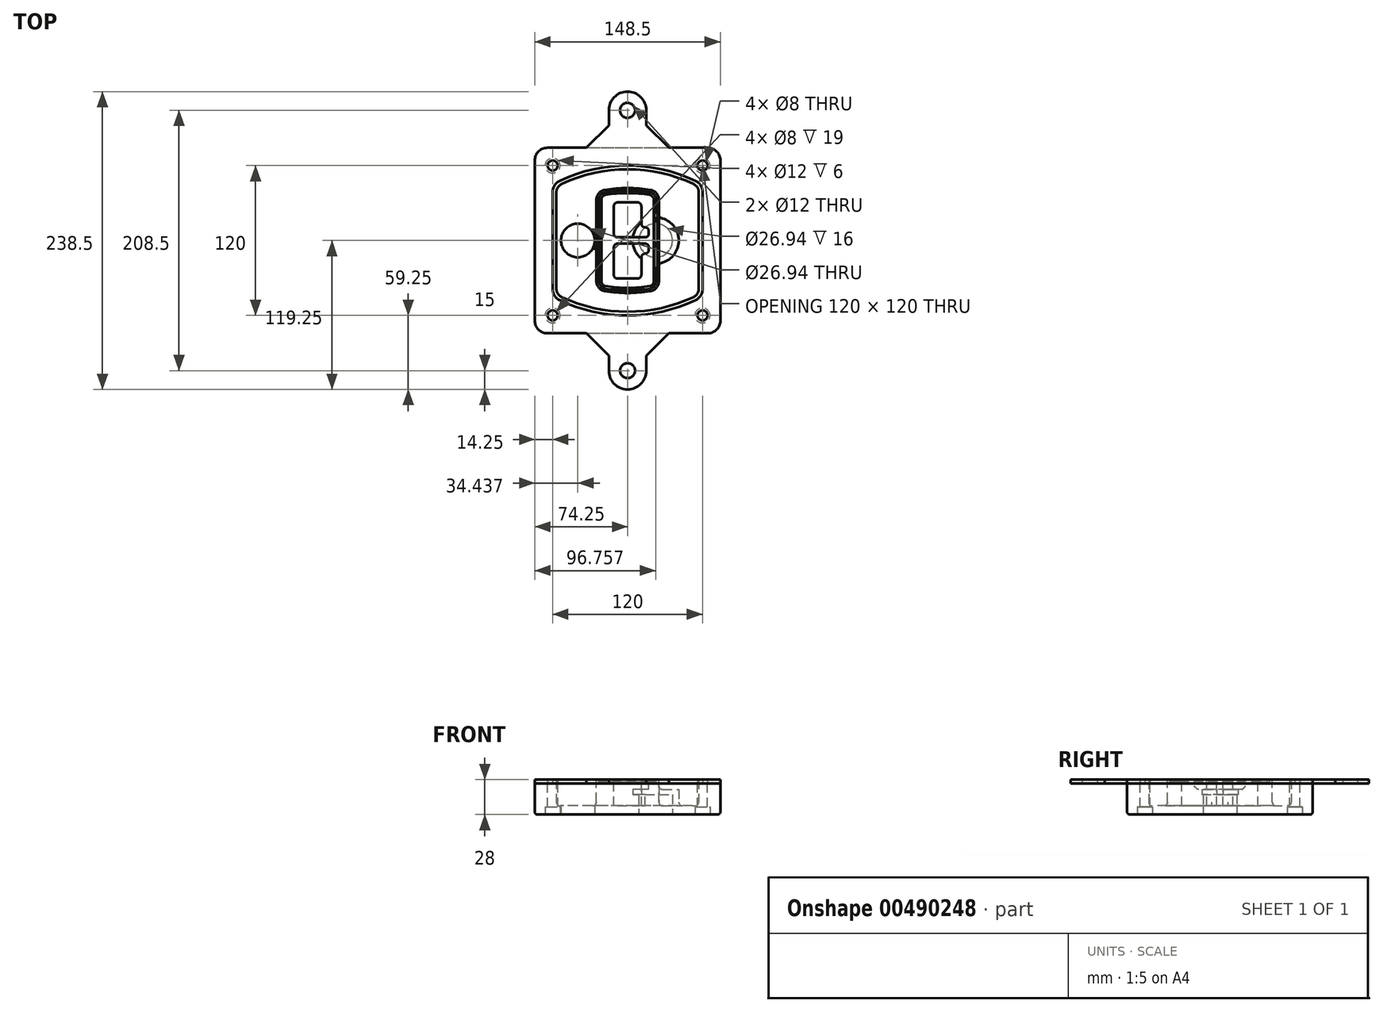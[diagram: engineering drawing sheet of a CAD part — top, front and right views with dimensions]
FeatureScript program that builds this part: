
annotation { "Feature Type Name" : "Feature", "Feature Type Description" : "" }
export const myFeature = defineFeature(function(context is Context, id is Id, definition is map)
    precondition{}
    {
        {
            var Q0;
            Q0=qCreatedBy(makeId("Top.planeOp"),FACE);
            var sketch = newSketch(context, id + "F0", { "sketchPlane" : qUnion([Q0])});
            skPoint(sketch, "E0.rect.middle", {"position": v(0, 0) * mm});
            skLineSegment(sketch, "E1.bottom", {"start": v(-64.25, -74.25) * mm, "end": v(64.25, -74.25) * mm});
            skLineSegment(sketch, "E1.top", {"start": v(-64.25, 74.25) * mm, "end": v(64.25, 74.25) * mm});
            skLineSegment(sketch, "E1.left", {"start": v(-74.25, -64.25) * mm, "end": v(-74.25, 64.25) * mm});
            skLineSegment(sketch, "E1.right", {"start": v(74.25, -64.25) * mm, "end": v(74.25, 64.25) * mm});
            skLineSegment(sketch, "E2", {"start": v(-74.25, 74.25) * mm, "end": v(74.25, -74.25) * mm, "construction": true});
            skLineSegment(sketch, "E3", {"start": v(74.25, 74.25) * mm, "end": v(-74.25, -74.25) * mm, "construction": true});
            skCircle(sketch, "E4", {"center": v(-60, 60) * mm, "radius": 4 * mm});
            skCircle(sketch, "E5", {"center": v(60, 60) * mm, "radius": 4 * mm});
            skCircle(sketch, "E6", {"center": v(60, -60) * mm, "radius": 4 * mm});
            skCircle(sketch, "E7", {"center": v(-60, -60) * mm, "radius": 4 * mm});
            skLineSegment(sketch, "E8", {"start": v(-60, 60) * mm, "end": v(60, 60) * mm, "construction": true});
            skLineSegment(sketch, "E9", {"start": v(60, 60) * mm, "end": v(60, -60) * mm, "construction": true});
            skLineSegment(sketch, "E10", {"start": v(60, -60) * mm, "end": v(-60, -60) * mm, "construction": true});
            skLineSegment(sketch, "E11", {"start": v(-60, -60) * mm, "end": v(-60, 60) * mm, "construction": true});
            skLineSegment(sketch, "E12", {"start": v(-60, 38.83) * mm, "end": v(-60, -38.83) * mm});
            skLineSegment(sketch, "E13", {"start": v(60, 38.83) * mm, "end": v(60, -38.83) * mm});
            skArc(sketch, "E14", {"start": v(54.26, 47.88) * mm, "mid": v(0, 60) * mm, "end": v(-54.26, 47.88) * mm});
            skArc(sketch, "E15", {"start": v(-54.26, -47.88) * mm, "mid": v(0, -60) * mm, "end": v(54.26, -47.88) * mm});
            skLineSegment(sketch, "E16", {"start": v(-60, 0) * mm, "end": v(60, 0) * mm, "construction": true});
            skPoint(sketch, "E17.visualSharp", {"position": v(-60, -45) * mm});
            skArc(sketch, "E17.filletArc", {"start": v(-60, -38.83) * mm, "mid": v(-58.44, -44.2) * mm, "end": v(-54.26, -47.88) * mm});
            skPoint(sketch, "E18.visualSharp", {"position": v(-60, 45) * mm});
            skArc(sketch, "E18.filletArc", {"start": v(-54.26, 47.88) * mm, "mid": v(-58.44, 44.2) * mm, "end": v(-60, 38.83) * mm});
            skPoint(sketch, "E19.visualSharp", {"position": v(60, 45) * mm});
            skArc(sketch, "E19.filletArc", {"start": v(60, 38.83) * mm, "mid": v(58.44, 44.2) * mm, "end": v(54.26, 47.88) * mm});
            skPoint(sketch, "E20.visualSharp", {"position": v(60, -45) * mm});
            skArc(sketch, "E20.filletArc", {"start": v(54.26, -47.88) * mm, "mid": v(58.44, -44.2) * mm, "end": v(60, -38.83) * mm});
            skPoint(sketch, "E21.visualSharp", {"position": v(-74.25, 74.25) * mm});
            skArc(sketch, "E21.filletArc", {"start": v(-64.25, 74.25) * mm, "mid": v(-71.32, 71.32) * mm, "end": v(-74.25, 64.25) * mm});
            skPoint(sketch, "E22.visualSharp", {"position": v(74.25, 74.25) * mm});
            skArc(sketch, "E22.filletArc", {"start": v(74.25, 64.25) * mm, "mid": v(71.32, 71.32) * mm, "end": v(64.25, 74.25) * mm});
            skPoint(sketch, "E23.visualSharp", {"position": v(74.25, -74.25) * mm});
            skArc(sketch, "E23.filletArc", {"start": v(64.25, -74.25) * mm, "mid": v(71.32, -71.32) * mm, "end": v(74.25, -64.25) * mm});
            skPoint(sketch, "E24.visualSharp", {"position": v(-74.25, -74.25) * mm});
            skArc(sketch, "E24.filletArc", {"start": v(-74.25, -64.25) * mm, "mid": v(-71.32, -71.32) * mm, "end": v(-64.25, -74.25) * mm});
            skArc(sketch, "E25.0", {"start": v(57, 38.83) * mm, "mid": v(55.9, 42.58) * mm, "end": v(52.98, 45.17) * mm});
            skLineSegment(sketch, "E25.1", {"start": v(57, 38.83) * mm, "end": v(57, -38.83) * mm});
            skArc(sketch, "E25.2", {"start": v(52.98, -45.17) * mm, "mid": v(55.9, -42.58) * mm, "end": v(57, -38.83) * mm});
            skArc(sketch, "E25.3", {"start": v(-52.98, -45.17) * mm, "mid": v(0, -57) * mm, "end": v(52.98, -45.17) * mm});
            skArc(sketch, "E25.4", {"start": v(-57, -38.83) * mm, "mid": v(-55.9, -42.58) * mm, "end": v(-52.98, -45.17) * mm});
            skArc(sketch, "E25.5", {"start": v(52.98, 45.17) * mm, "mid": v(0, 57) * mm, "end": v(-52.98, 45.17) * mm});
            skLineSegment(sketch, "E25.6", {"start": v(-57, 38.83) * mm, "end": v(-57, -38.83) * mm});
            skArc(sketch, "E25.7", {"start": v(-52.98, 45.17) * mm, "mid": v(-55.9, 42.58) * mm, "end": v(-57, 38.83) * mm});
            skArc(sketch, "E26.0", {"start": v(-55.96, 51.5) * mm, "mid": v(-61.82, 46.33) * mm, "end": v(-64, 38.83) * mm});
            skArc(sketch, "E26.1", {"start": v(55.96, 51.5) * mm, "mid": v(0, 64) * mm, "end": v(-55.96, 51.5) * mm});
            skArc(sketch, "E26.2", {"start": v(64, 38.83) * mm, "mid": v(61.82, 46.33) * mm, "end": v(55.96, 51.5) * mm});
            skLineSegment(sketch, "E26.3", {"start": v(64, 38.83) * mm, "end": v(64, -38.83) * mm});
            skArc(sketch, "E26.4", {"start": v(55.96, -51.5) * mm, "mid": v(61.82, -46.33) * mm, "end": v(64, -38.83) * mm});
            skLineSegment(sketch, "E26.5", {"start": v(-64, 38.83) * mm, "end": v(-64, -38.83) * mm});
            skArc(sketch, "E26.6", {"start": v(-55.96, -51.5) * mm, "mid": v(0, -64) * mm, "end": v(55.96, -51.5) * mm});
            skArc(sketch, "E26.7", {"start": v(-64, -38.83) * mm, "mid": v(-61.82, -46.33) * mm, "end": v(-55.96, -51.5) * mm});
            skSolve(sketch);
        }
        {
            var Q0;
            Q0=makeQuery(id+"F0.imprint","IMPRINT",FACE,{"disambiguationData":[TD([[makeQuery(id+"F0.imprint","IMPRINT",EDGE,{"derivedFrom":sQuery(id+"F0.wireOp",EDGE,"E1.bottom")}),1.0]])]});
            var Q1;
            Q1=makeQuery(id+"F0.imprint","IMPRINT",FACE,{"disambiguationData":[TD([[makeQuery(id+"F0.imprint","IMPRINT",EDGE,{"derivedFrom":sQuery(id+"F0.wireOp",EDGE,"E12")}),1.0]])]});
            var Q2;
            Q2=makeQuery(id+"F0.imprint","IMPRINT",FACE,{"disambiguationData":[TD([[makeQuery(id+"F0.imprint","IMPRINT",EDGE,{"derivedFrom":sQuery(id+"F0.wireOp",EDGE,"E25.0")}),1.0]])]});
            var Q3;
            Q3=makeQuery(id+"F0.imprint","IMPRINT",FACE,{"disambiguationData":[TD([[makeQuery(id+"F0.imprint","IMPRINT",EDGE,{"derivedFrom":sQuery(id+"F0.wireOp",EDGE,"E12")}),-1.0]])]});
            extrude(context, id + "F1", {"entities" : qUnion([Q0, Q1, Q2, Q3]), "oppositeDirection" : true, "depth" : 25 * mm});
        }
        {
            var Q0;
            Q0=makeQuery(id+"F0.imprint","IMPRINT",FACE,{"disambiguationData":[TD([[makeQuery(id+"F0.imprint","IMPRINT",EDGE,{"derivedFrom":sQuery(id+"F0.wireOp",EDGE,"E12")}),1.0]])]});
            extrude(context, id + "F2", {"entities" : qUnion([Q0]), "operationType" : NewBodyOperationType.ADD, "depth" : 3 * mm});
        }
        {
            var Q0;
            Q0=makeQuery(id+"F0.imprint","IMPRINT",FACE,{"disambiguationData":[TD([[makeQuery(id+"F0.imprint","IMPRINT",EDGE,{"derivedFrom":sQuery(id+"F0.wireOp",EDGE,"E25.0")}),1.0]])]});
            extrude(context, id + "F3", {"entities" : qUnion([Q0]), "operationType" : NewBodyOperationType.REMOVE, "oppositeDirection" : true, "depth" : 18 * mm});
        }
        {
            var Q0;
            Q0=makeQuery(id+"F2.opExtrude","CAP_FACE",FACE,{"disambiguationData":[OSD([sQuery(id+"F0.wireOp",EDGE,"E12"),sQuery(id+"F0.wireOp",EDGE,"E13"),sQuery(id+"F0.wireOp",EDGE,"E14"),sQuery(id+"F0.wireOp",EDGE,"E15"),sQuery(id+"F0.wireOp",EDGE,"E17.filletArc"),sQuery(id+"F0.wireOp",EDGE,"E18.filletArc"),sQuery(id+"F0.wireOp",EDGE,"E19.filletArc"),sQuery(id+"F0.wireOp",EDGE,"E20.filletArc"),sQuery(id+"F0.wireOp",EDGE,"E25.0"),sQuery(id+"F0.wireOp",EDGE,"E25.1"),sQuery(id+"F0.wireOp",EDGE,"E25.2"),sQuery(id+"F0.wireOp",EDGE,"E25.3"),sQuery(id+"F0.wireOp",EDGE,"E25.4"),sQuery(id+"F0.wireOp",EDGE,"E25.5"),sQuery(id+"F0.wireOp",EDGE,"E25.6"),sQuery(id+"F0.wireOp",EDGE,"E25.7")])],"isStart":false});
            var sketch = newSketch(context, id + "F4", { "sketchPlane" : qUnion([Q0])});
            skArc(sketch, "E27.0", {"start": v(-18.34, -40.45) * mm, "mid": v(0, -42) * mm, "end": v(18.34, -40.45) * mm});
            skArc(sketch, "E28.0", {"start": v(18.34, 40.45) * mm, "mid": v(0, 42) * mm, "end": v(-18.34, 40.45) * mm});
            skLineSegment(sketch, "E29", {"start": v(-25, 32.57) * mm, "end": v(-25, -32.57) * mm});
            skLineSegment(sketch, "E30", {"start": v(25, 32.57) * mm, "end": v(25, -32.57) * mm});
            skLineSegment(sketch, "E31", {"start": v(-25, 39.1) * mm, "end": v(25, 39.1) * mm, "construction": true});
            skLineSegment(sketch, "E32", {"start": v(-25, -39.1) * mm, "end": v(25, -39.1) * mm, "construction": true});
            skPoint(sketch, "E33.visualSharp", {"position": v(-25, 39.1) * mm});
            skArc(sketch, "E33.filletArc", {"start": v(-18.34, 40.45) * mm, "mid": v(-23.11, 37.73) * mm, "end": v(-25, 32.57) * mm});
            skPoint(sketch, "E34.visualSharp", {"position": v(25, 39.1) * mm});
            skArc(sketch, "E34.filletArc", {"start": v(25, 32.57) * mm, "mid": v(23.11, 37.73) * mm, "end": v(18.34, 40.45) * mm});
            skPoint(sketch, "E35.visualSharp", {"position": v(25, -39.1) * mm});
            skArc(sketch, "E35.filletArc", {"start": v(18.34, -40.45) * mm, "mid": v(23.11, -37.73) * mm, "end": v(25, -32.57) * mm});
            skPoint(sketch, "E36.visualSharp", {"position": v(-25, -39.1) * mm});
            skArc(sketch, "E36.filletArc", {"start": v(-25, -32.57) * mm, "mid": v(-23.11, -37.73) * mm, "end": v(-18.34, -40.45) * mm});
            skArc(sketch, "E37.0", {"start": v(52.98, 45.17) * mm, "mid": v(0, 57) * mm, "end": v(-52.98, 45.17) * mm});
            skArc(sketch, "E37.1", {"start": v(-52.98, 45.17) * mm, "mid": v(-55.9, 42.58) * mm, "end": v(-57, 38.83) * mm});
            skLineSegment(sketch, "E37.2", {"start": v(-57, 38.83) * mm, "end": v(-57, -38.83) * mm});
            skArc(sketch, "E37.3", {"start": v(-57, -38.83) * mm, "mid": v(-55.9, -42.58) * mm, "end": v(-52.98, -45.17) * mm});
            skArc(sketch, "E37.4", {"start": v(-52.98, -45.17) * mm, "mid": v(0, -57) * mm, "end": v(52.98, -45.17) * mm});
            skArc(sketch, "E37.5", {"start": v(52.98, -45.17) * mm, "mid": v(55.9, -42.58) * mm, "end": v(57, -38.83) * mm});
            skLineSegment(sketch, "E37.6", {"start": v(57, 38.83) * mm, "end": v(57, -38.83) * mm});
            skArc(sketch, "E37.7", {"start": v(57, 38.83) * mm, "mid": v(55.9, 42.58) * mm, "end": v(52.98, 45.17) * mm});
            skLineSegment(sketch, "E38.0", {"start": v(23, 32.57) * mm, "end": v(23, -32.57) * mm});
            skArc(sketch, "E38.1", {"start": v(18, -38.48) * mm, "mid": v(21.58, -36.44) * mm, "end": v(23, -32.57) * mm});
            skArc(sketch, "E38.2", {"start": v(-18, -38.48) * mm, "mid": v(0, -40) * mm, "end": v(18, -38.48) * mm});
            skArc(sketch, "E38.3", {"start": v(-23, -32.57) * mm, "mid": v(-21.58, -36.44) * mm, "end": v(-18, -38.48) * mm});
            skLineSegment(sketch, "E38.4", {"start": v(-23, 32.57) * mm, "end": v(-23, -32.57) * mm});
            skArc(sketch, "E38.5", {"start": v(23, 32.57) * mm, "mid": v(21.58, 36.44) * mm, "end": v(18, 38.48) * mm});
            skArc(sketch, "E38.6", {"start": v(-18, 38.48) * mm, "mid": v(-21.58, 36.44) * mm, "end": v(-23, 32.57) * mm});
            skArc(sketch, "E38.7", {"start": v(18, 38.48) * mm, "mid": v(0, 40) * mm, "end": v(-18, 38.48) * mm});
            skArc(sketch, "E39.0", {"start": v(21, 32.57) * mm, "mid": v(20.06, 35.15) * mm, "end": v(17.67, 36.5) * mm});
            skLineSegment(sketch, "E39.1", {"start": v(21, 32.57) * mm, "end": v(21, -32.57) * mm});
            skArc(sketch, "E39.2", {"start": v(17.67, -36.5) * mm, "mid": v(20.06, -35.15) * mm, "end": v(21, -32.57) * mm});
            skArc(sketch, "E39.3", {"start": v(-17.67, -36.5) * mm, "mid": v(0, -38) * mm, "end": v(17.67, -36.5) * mm});
            skArc(sketch, "E39.4", {"start": v(-21, -32.57) * mm, "mid": v(-20.06, -35.15) * mm, "end": v(-17.67, -36.5) * mm});
            skArc(sketch, "E39.5", {"start": v(17.67, 36.5) * mm, "mid": v(0, 38) * mm, "end": v(-17.67, 36.5) * mm});
            skLineSegment(sketch, "E39.6", {"start": v(-21, 32.57) * mm, "end": v(-21, -32.57) * mm});
            skArc(sketch, "E39.7", {"start": v(-17.67, 36.5) * mm, "mid": v(-20.06, 35.15) * mm, "end": v(-21, 32.57) * mm});
            skLineSegment(sketch, "E40", {"start": v(-25, 0) * mm, "end": v(25, 0) * mm, "construction": true});
            skLineSegment(sketch, "E41", {"start": v(-11, 5.5) * mm, "end": v(-11, 27.5) * mm});
            skLineSegment(sketch, "E42", {"start": v(-8, 30.5) * mm, "end": v(8, 30.5) * mm});
            skLineSegment(sketch, "E43", {"start": v(11, 27.5) * mm, "end": v(11, 13.5) * mm});
            skLineSegment(sketch, "E44", {"start": v(14, 10.5) * mm, "end": v(14, 10.5) * mm});
            skLineSegment(sketch, "E45", {"start": v(17, 7.5) * mm, "end": v(17, 5.5) * mm});
            skLineSegment(sketch, "E46", {"start": v(14, 2.5) * mm, "end": v(-8, 2.5) * mm});
            skPoint(sketch, "E47.visualSharp", {"position": v(-11, 30.5) * mm});
            skArc(sketch, "E47.filletArc", {"start": v(-8, 30.5) * mm, "mid": v(-10.12, 29.62) * mm, "end": v(-11, 27.5) * mm});
            skPoint(sketch, "E48.visualSharp", {"position": v(11, 30.5) * mm});
            skArc(sketch, "E48.filletArc", {"start": v(11, 27.5) * mm, "mid": v(10.12, 29.62) * mm, "end": v(8, 30.5) * mm});
            skPoint(sketch, "E49.visualSharp", {"position": v(11, 10.5) * mm});
            skArc(sketch, "E49.filletArc", {"start": v(11, 13.5) * mm, "mid": v(11.88, 11.38) * mm, "end": v(14, 10.5) * mm});
            skPoint(sketch, "E50.visualSharp", {"position": v(17, 10.5) * mm});
            skArc(sketch, "E50.filletArc", {"start": v(17, 7.5) * mm, "mid": v(16.12, 9.62) * mm, "end": v(14, 10.5) * mm});
            skPoint(sketch, "E51.visualSharp", {"position": v(17, 2.5) * mm});
            skArc(sketch, "E51.filletArc", {"start": v(14, 2.5) * mm, "mid": v(16.12, 3.38) * mm, "end": v(17, 5.5) * mm});
            skPoint(sketch, "E52.visualSharp", {"position": v(-11, 2.5) * mm});
            skArc(sketch, "E52.filletArc", {"start": v(-11, 5.5) * mm, "mid": v(-10.12, 3.38) * mm, "end": v(-8, 2.5) * mm});
            skLineSegment(sketch, "E53.0.MirrorCS", {"start": v(14, -2.5) * mm, "end": v(-8, -2.5) * mm});
            skArc(sketch, "E54.0.MirrorCS", {"start": v(-11, -5.5) * mm, "mid": v(-10.12, -3.38) * mm, "end": v(-8, -2.5) * mm});
            skLineSegment(sketch, "E55.0.MirrorCS", {"start": v(-11, -5.5) * mm, "end": v(-11, -27.5) * mm});
            skArc(sketch, "E56.0.MirrorCS", {"start": v(-8, -30.5) * mm, "mid": v(-10.12, -29.62) * mm, "end": v(-11, -27.5) * mm});
            skLineSegment(sketch, "E57.0.MirrorCS", {"start": v(-8, -30.5) * mm, "end": v(8, -30.5) * mm});
            skArc(sketch, "E58.0.MirrorCS", {"start": v(11, -27.5) * mm, "mid": v(10.12, -29.62) * mm, "end": v(8, -30.5) * mm});
            skLineSegment(sketch, "E59.0.MirrorCS", {"start": v(11, -27.5) * mm, "end": v(11, -13.5) * mm});
            skArc(sketch, "E60.0.MirrorCS", {"start": v(11, -13.5) * mm, "mid": v(11.88, -11.38) * mm, "end": v(14, -10.5) * mm});
            skArc(sketch, "E61.0.MirrorCS", {"start": v(17, -7.5) * mm, "mid": v(16.12, -9.62) * mm, "end": v(14, -10.5) * mm});
            skLineSegment(sketch, "E62.0.MirrorCS", {"start": v(17, -7.5) * mm, "end": v(17, -5.5) * mm});
            skArc(sketch, "E63.0.MirrorCS", {"start": v(14, -2.5) * mm, "mid": v(16.12, -3.38) * mm, "end": v(17, -5.5) * mm});
            skSolve(sketch);
        }
        {
            var Q0;
            Q0=makeQuery(id+"F4.imprint","IMPRINT",FACE,{"disambiguationData":[TD([[makeQuery(id+"F4.imprint","IMPRINT",EDGE,{"derivedFrom":sQuery(id+"F4.wireOp",EDGE,"E27.0")}),1.0]])]});
            var Q1;
            Q1=makeQuery(id+"F4.imprint","IMPRINT",FACE,{"disambiguationData":[TD([[makeQuery(id+"F4.imprint","IMPRINT",EDGE,{"derivedFrom":sQuery(id+"F4.wireOp",EDGE,"E38.0")}),-1.0]])]});
            var Q2;
            Q2=makeQuery(id+"F4.imprint","IMPRINT",FACE,{"disambiguationData":[TD([[makeQuery(id+"F4.imprint","IMPRINT",EDGE,{"derivedFrom":sQuery(id+"F4.wireOp",EDGE,"E39.0")}),1.0]])]});
            extrude(context, id + "F5", {"entities" : qUnion([Q0, Q1, Q2]), "operationType" : NewBodyOperationType.ADD, "endBound" : BoundingType.UP_TO_NEXT, "oppositeDirection" : true, "depth" : 25 * mm});
        }
        {
            var Q0;
            Q0=makeQuery(id+"F4.imprint","IMPRINT",FACE,{"disambiguationData":[TD([[makeQuery(id+"F4.imprint","IMPRINT",EDGE,{"derivedFrom":sQuery(id+"F4.wireOp",EDGE,"E38.0")}),-1.0]])]});
            extrude(context, id + "F6", {"entities" : qUnion([Q0]), "operationType" : NewBodyOperationType.REMOVE, "oppositeDirection" : true, "depth" : 2 * mm});
        }
        {
            var Q0;
            Q0=makeQuery(id+"F1.opExtrude","CAP_FACE",FACE,{"disambiguationData":[OSD([sQuery(id+"F0.wireOp",EDGE,"E1.bottom"),sQuery(id+"F0.wireOp",EDGE,"E1.top"),sQuery(id+"F0.wireOp",EDGE,"E1.left"),sQuery(id+"F0.wireOp",EDGE,"E1.right"),sQuery(id+"F0.wireOp",EDGE,"E4"),sQuery(id+"F0.wireOp",EDGE,"E5"),sQuery(id+"F0.wireOp",EDGE,"E6"),sQuery(id+"F0.wireOp",EDGE,"E7"),sQuery(id+"F0.wireOp",EDGE,"E21.filletArc"),sQuery(id+"F0.wireOp",EDGE,"E22.filletArc"),sQuery(id+"F0.wireOp",EDGE,"E23.filletArc"),sQuery(id+"F0.wireOp",EDGE,"E24.filletArc")])],"isStart":false});
            var sketch = newSketch(context, id + "F7", { "sketchPlane" : qUnion([Q0])});
            skCircle(sketch, "E64", {"center": v(22.5, 0) * mm, "radius": 13.47 * mm});
            skCircle(sketch, "E65", {"center": v(-39.81, 0) * mm, "radius": 13.47 * mm});
            skLineSegment(sketch, "E66", {"start": v(74.25, 0) * mm, "end": v(-74.25, 0) * mm});
            skCircle(sketch, "E67", {"center": v(22.5, 0) * mm, "radius": 18.47 * mm});
            skCircle(sketch, "E68", {"center": v(60, -60) * mm, "radius": 6 * mm});
            skCircle(sketch, "E69", {"center": v(-60, -60) * mm, "radius": 6 * mm});
            skCircle(sketch, "E70", {"center": v(-60, 60) * mm, "radius": 6 * mm});
            skCircle(sketch, "E71", {"center": v(60, 60) * mm, "radius": 6 * mm});
            skSolve(sketch);
        }
        {
            var Q0;
            {var subQ1=sQuery(id+"F7.wireOp",EDGE,"E66");var subQ4=sQuery(id+"F7.wireOp",EDGE,"E64");var subQ6=makeQuery(id+"F7.imprint","INTERSECT",VERTEX,{"disambiguationData":[OD(0.0)],"derivedFrom":[subQ4,subQ1]});Q0=makeQuery(id+"F7.imprint","IMPRINT",FACE,{"disambiguationData":[TD([[makeQuery(id+"F7.imprint","IMPRINT",EDGE,{"disambiguationData":[TD([[subQ6,-1.0]])],"derivedFrom":subQ4}),-1.0]])]});}
            var Q1;
            {var subQ0=sQuery(id+"F7.wireOp",EDGE,"E66");var subQ1=sQuery(id+"F7.wireOp",EDGE,"E64");var subQ3=makeQuery(id+"F7.imprint","INTERSECT",VERTEX,{"disambiguationData":[OD(0.0)],"derivedFrom":[subQ1,subQ0]});Q1=makeQuery(id+"F7.imprint","IMPRINT",FACE,{"disambiguationData":[TD([[makeQuery(id+"F7.imprint","IMPRINT",EDGE,{"disambiguationData":[TD([[subQ3,-1.0]])],"derivedFrom":subQ1}),1.0]])]});}
            var Q2;
            {var subQ0=sQuery(id+"F7.wireOp",EDGE,"E66");var subQ1=sQuery(id+"F7.wireOp",EDGE,"E64");var subQ3=makeQuery(id+"F7.imprint","INTERSECT",VERTEX,{"disambiguationData":[OD(0.0)],"derivedFrom":[subQ1,subQ0]});Q2=makeQuery(id+"F7.imprint","IMPRINT",FACE,{"disambiguationData":[TD([[makeQuery(id+"F7.imprint","IMPRINT",EDGE,{"disambiguationData":[TD([[subQ3,1.0]])],"derivedFrom":subQ1}),1.0]])]});}
            var Q3;
            {var subQ1=sQuery(id+"F7.wireOp",EDGE,"E66");var subQ4=sQuery(id+"F7.wireOp",EDGE,"E64");var subQ6=makeQuery(id+"F7.imprint","INTERSECT",VERTEX,{"disambiguationData":[OD(0.0)],"derivedFrom":[subQ4,subQ1]});Q3=makeQuery(id+"F7.imprint","IMPRINT",FACE,{"disambiguationData":[TD([[makeQuery(id+"F7.imprint","IMPRINT",EDGE,{"disambiguationData":[TD([[subQ6,1.0]])],"derivedFrom":subQ4}),-1.0]])]});}
            extrude(context, id + "F8", {"entities" : qUnion([Q0, Q1, Q2, Q3]), "operationType" : NewBodyOperationType.ADD, "oppositeDirection" : true, "depth" : 20 * mm});
        }
        {
            var Q0;
            {var subQ0=sQuery(id+"F7.wireOp",EDGE,"E66");var subQ1=sQuery(id+"F7.wireOp",EDGE,"E64");var subQ3=makeQuery(id+"F7.imprint","INTERSECT",VERTEX,{"disambiguationData":[OD(0.0)],"derivedFrom":[subQ1,subQ0]});Q0=makeQuery(id+"F7.imprint","IMPRINT",FACE,{"disambiguationData":[TD([[makeQuery(id+"F7.imprint","IMPRINT",EDGE,{"disambiguationData":[TD([[subQ3,-1.0]])],"derivedFrom":subQ1}),1.0]])]});}
            var Q1;
            {var subQ0=sQuery(id+"F7.wireOp",EDGE,"E66");var subQ1=sQuery(id+"F7.wireOp",EDGE,"E64");var subQ3=makeQuery(id+"F7.imprint","INTERSECT",VERTEX,{"disambiguationData":[OD(0.0)],"derivedFrom":[subQ1,subQ0]});Q1=makeQuery(id+"F7.imprint","IMPRINT",FACE,{"disambiguationData":[TD([[makeQuery(id+"F7.imprint","IMPRINT",EDGE,{"disambiguationData":[TD([[subQ3,1.0]])],"derivedFrom":subQ1}),1.0]])]});}
            extrude(context, id + "F9", {"entities" : qUnion([Q0, Q1]), "operationType" : NewBodyOperationType.REMOVE, "oppositeDirection" : true, "depth" : 16 * mm});
        }
        {
            var Q0;
            {var subQ0=sQuery(id+"F7.wireOp",EDGE,"E66");var subQ1=sQuery(id+"F7.wireOp",EDGE,"E65");var subQ3=makeQuery(id+"F7.imprint","INTERSECT",VERTEX,{"disambiguationData":[OD(0.0)],"derivedFrom":[subQ1,subQ0]});Q0=makeQuery(id+"F7.imprint","IMPRINT",FACE,{"disambiguationData":[TD([[makeQuery(id+"F7.imprint","IMPRINT",EDGE,{"disambiguationData":[TD([[subQ3,-1.0]])],"derivedFrom":subQ1}),1.0]])]});}
            var Q1;
            {var subQ0=sQuery(id+"F7.wireOp",EDGE,"E66");var subQ1=sQuery(id+"F7.wireOp",EDGE,"E65");var subQ3=makeQuery(id+"F7.imprint","INTERSECT",VERTEX,{"disambiguationData":[OD(0.0)],"derivedFrom":[subQ1,subQ0]});Q1=makeQuery(id+"F7.imprint","IMPRINT",FACE,{"disambiguationData":[TD([[makeQuery(id+"F7.imprint","IMPRINT",EDGE,{"disambiguationData":[TD([[subQ3,1.0]])],"derivedFrom":subQ1}),1.0]])]});}
            extrude(context, id + "F10", {"entities" : qUnion([Q0, Q1]), "operationType" : NewBodyOperationType.REMOVE, "oppositeDirection" : true, "depth" : 25 * mm});
        }
        {
            var Q0;
            Q0=makeQuery(id+"F7.imprint","IMPRINT",FACE,{"disambiguationData":[TD([[makeQuery(id+"F7.imprint","IMPRINT",EDGE,{"derivedFrom":sQuery(id+"F7.wireOp",EDGE,"E68")}),1.0]])]});
            var Q1;
            Q1=makeQuery(id+"F7.imprint","IMPRINT",FACE,{"disambiguationData":[TD([[makeQuery(id+"F7.imprint","IMPRINT",EDGE,{"derivedFrom":makeQuery(id+"F1.opExtrude","CAP_EDGE",EDGE,{"disambiguationData":[OSD([sQuery(id+"F0.wireOp",EDGE,"E5")])],"isStart":false})}),-1.0]])]});
            var Q2;
            Q2=makeQuery(id+"F7.imprint","IMPRINT",FACE,{"disambiguationData":[TD([[makeQuery(id+"F7.imprint","IMPRINT",EDGE,{"derivedFrom":sQuery(id+"F7.wireOp",EDGE,"E69")}),1.0]])]});
            var Q3;
            Q3=makeQuery(id+"F7.imprint","IMPRINT",FACE,{"disambiguationData":[TD([[makeQuery(id+"F7.imprint","IMPRINT",EDGE,{"derivedFrom":makeQuery(id+"F1.opExtrude","CAP_EDGE",EDGE,{"disambiguationData":[OSD([sQuery(id+"F0.wireOp",EDGE,"E4")])],"isStart":false})}),-1.0]])]});
            var Q4;
            Q4=makeQuery(id+"F7.imprint","IMPRINT",FACE,{"disambiguationData":[TD([[makeQuery(id+"F7.imprint","IMPRINT",EDGE,{"derivedFrom":sQuery(id+"F7.wireOp",EDGE,"E70")}),1.0]])]});
            var Q5;
            Q5=makeQuery(id+"F7.imprint","IMPRINT",FACE,{"disambiguationData":[TD([[makeQuery(id+"F7.imprint","IMPRINT",EDGE,{"derivedFrom":makeQuery(id+"F1.opExtrude","CAP_EDGE",EDGE,{"disambiguationData":[OSD([sQuery(id+"F0.wireOp",EDGE,"E7")])],"isStart":false})}),-1.0]])]});
            var Q6;
            Q6=makeQuery(id+"F7.imprint","IMPRINT",FACE,{"disambiguationData":[TD([[makeQuery(id+"F7.imprint","IMPRINT",EDGE,{"derivedFrom":sQuery(id+"F7.wireOp",EDGE,"E71")}),1.0]])]});
            var Q7;
            Q7=makeQuery(id+"F7.imprint","IMPRINT",FACE,{"disambiguationData":[TD([[makeQuery(id+"F7.imprint","IMPRINT",EDGE,{"derivedFrom":makeQuery(id+"F1.opExtrude","CAP_EDGE",EDGE,{"disambiguationData":[OSD([sQuery(id+"F0.wireOp",EDGE,"E6")])],"isStart":false})}),-1.0]])]});
            extrude(context, id + "F11", {"entities" : qUnion([Q0, Q1, Q2, Q3, Q4, Q5, Q6, Q7]), "operationType" : NewBodyOperationType.REMOVE, "oppositeDirection" : true, "depth" : 6 * mm});
        }
        {
            var Q0;
            Q0=makeQuery(id+"F9.boolean.opBoolean","COPY",FACE,{"derivedFrom":makeQuery(id+"F9.opExtrude","CAP_FACE",FACE,{"disambiguationData":[OSD([sQuery(id+"F7.wireOp",EDGE,"E64")])],"isStart":false})});
            var sketch = newSketch(context, id + "F12", { "sketchPlane" : qUnion([Q0])});
            skArc(sketch, "E72.0", {"start": v(11, 14.45) * mm, "mid": v(6.45, 9.13) * mm, "end": v(4.2, 2.5) * mm});
            skArc(sketch, "E72.1", {"start": v(4.2, -2.5) * mm, "mid": v(6.45, -9.13) * mm, "end": v(11, -14.45) * mm});
            skLineSegment(sketch, "E73", {"start": v(4.2, -2.5) * mm, "end": v(14, -2.5) * mm});
            skLineSegment(sketch, "E74.0", {"start": v(14, 2.5) * mm, "end": v(4.2, 2.5) * mm});
            skArc(sketch, "E74.1", {"start": v(14, 2.5) * mm, "mid": v(16.12, 3.38) * mm, "end": v(17, 5.5) * mm});
            skLineSegment(sketch, "E74.2", {"start": v(17, 7.5) * mm, "end": v(17, 5.5) * mm});
            skArc(sketch, "E74.3", {"start": v(17, 7.5) * mm, "mid": v(16.12, 9.62) * mm, "end": v(14, 10.5) * mm});
            skArc(sketch, "E74.4", {"start": v(11, 13.5) * mm, "mid": v(11.88, 11.38) * mm, "end": v(14, 10.5) * mm});
            skLineSegment(sketch, "E74.5", {"start": v(11, 14.45) * mm, "end": v(11, 13.5) * mm});
            skLineSegment(sketch, "E74.7", {"start": v(14, -2.5) * mm, "end": v(4.2, -2.5) * mm});
            skArc(sketch, "E74.8", {"start": v(14, -2.5) * mm, "mid": v(16.12, -3.38) * mm, "end": v(17, -5.5) * mm});
            skLineSegment(sketch, "E74.9", {"start": v(17, -7.5) * mm, "end": v(17, -5.5) * mm});
            skArc(sketch, "E74.10", {"start": v(17, -7.5) * mm, "mid": v(16.12, -9.62) * mm, "end": v(14, -10.5) * mm});
            skArc(sketch, "E74.11", {"start": v(11, -13.5) * mm, "mid": v(11.88, -11.38) * mm, "end": v(14, -10.5) * mm});
            skLineSegment(sketch, "E74.12", {"start": v(11, -14.45) * mm, "end": v(11, -13.5) * mm});
            skPoint(sketch, "E75.orphan", {"position": v(11, -27.5) * mm});
            skPoint(sketch, "E76.orphan", {"position": v(-8, -2.5) * mm});
            skPoint(sketch, "E77.orphan", {"position": v(-8, 2.5) * mm});
            skPoint(sketch, "E78.orphan", {"position": v(11, 27.5) * mm});
            skSolve(sketch);
        }
        {
            var Q0;
            {var subQ7=sQuery(id+"F12.wireOp",EDGE,"E72.0");var subQ14=sQuery(id+"F12.wireOp",EDGE,"E72.1");var subQ16=sQuery(id+"F12.wireOp",EDGE,"E74.1");var subQ18=sQuery(id+"F12.wireOp",EDGE,"E74.8");Q0=qUnion([makeQuery(id+"F12.imprint","IMPRINT",FACE,{"disambiguationData":[TD([[makeQuery(id+"F12.imprint","IMPRINT",EDGE,{"derivedFrom":subQ7}),1.0]])]}),makeQuery(id+"F12.imprint","IMPRINT",FACE,{"disambiguationData":[TD([[makeQuery(id+"F12.imprint","IMPRINT",EDGE,{"derivedFrom":subQ14}),1.0]])]}),makeQuery(id+"F12.imprint","IMPRINT",FACE,{"disambiguationData":[TD([[makeQuery(id+"F12.imprint","IMPRINT",EDGE,{"derivedFrom":subQ16}),1.0]])]}),makeQuery(id+"F12.imprint","IMPRINT",FACE,{"disambiguationData":[TD([[makeQuery(id+"F12.imprint","IMPRINT",EDGE,{"derivedFrom":subQ18}),-1.0]])]})]);}
            var Q1;
            Q1=makeQuery(id+"F5.boolean.opBoolean","SPLIT",FACE,{"disambiguationData":[TD([makeQuery(id+"F5.opExtrude","SWEPT_FACE",FACE,{"disambiguationData":[OSD([sQuery(id+"F4.wireOp",EDGE,"E41")])]})])],"derivedFrom":makeQuery(id+"F3.boolean.opBoolean","COPY",FACE,{"derivedFrom":makeQuery(id+"F3.opExtrude","CAP_FACE",FACE,{"disambiguationData":[OSD([sQuery(id+"F0.wireOp",EDGE,"E25.0"),sQuery(id+"F0.wireOp",EDGE,"E25.1"),sQuery(id+"F0.wireOp",EDGE,"E25.2"),sQuery(id+"F0.wireOp",EDGE,"E25.3"),sQuery(id+"F0.wireOp",EDGE,"E25.4"),sQuery(id+"F0.wireOp",EDGE,"E25.5"),sQuery(id+"F0.wireOp",EDGE,"E25.6"),sQuery(id+"F0.wireOp",EDGE,"E25.7")])],"isStart":false})})});
            extrude(context, id + "F13", {"entities" : qUnion([Q0]), "operationType" : NewBodyOperationType.REMOVE, "endBound" : BoundingType.UP_TO_SURFACE, "endBoundEntityFace" : qUnion([Q1]), "depth" : 25 * mm});
        }
        {
            var Q0;
            Q0=makeQuery(id+"F3.boolean.opBoolean","COPY",EDGE,{"derivedFrom":makeQuery(id+"F3.opExtrude","CAP_EDGE",EDGE,{"disambiguationData":[OSD([sQuery(id+"F0.wireOp",EDGE,"E25.6")])],"isStart":false})});
            var Q1;
            Q1=makeQuery(id+"F8.boolean.opBoolean","INTERSECT",EDGE,{"derivedFrom":[makeQuery(id+"F5.opExtrude","SWEPT_FACE",FACE,{"disambiguationData":[OSD([sQuery(id+"F4.wireOp",EDGE,"E30")])]}),makeQuery(id+"F8.opExtrude","CAP_FACE",FACE,{"disambiguationData":[OSD([sQuery(id+"F7.wireOp",EDGE,"E67")])],"isStart":false})]});
            var Q2;
            Q2=makeQuery(id+"F8.boolean.opBoolean","INTERSECT",EDGE,{"disambiguationData":[OD(1.0)],"derivedFrom":[makeQuery(id+"F5.opExtrude","SWEPT_FACE",FACE,{"disambiguationData":[OSD([sQuery(id+"F4.wireOp",EDGE,"E30")])]}),makeQuery(id+"F8.opExtrude","SWEPT_FACE",FACE,{"disambiguationData":[OSD([sQuery(id+"F7.wireOp",EDGE,"E67")])]})]});
            var Q3;
            {var subQ0=sQuery(id+"F4.wireOp",EDGE,"E30");Q3=makeQuery(id+"F8.boolean.opBoolean","SPLIT",EDGE,{"disambiguationData":[TD([makeQuery(id+"F5.opExtrude","SWEPT_FACE",FACE,{"disambiguationData":[OSD([sQuery(id+"F4.wireOp",EDGE,"E35.filletArc")])]})])],"derivedFrom":makeQuery(id+"F5.opExtrude","CAP_EDGE",EDGE,{"disambiguationData":[OSD([subQ0])],"isStart":false})});}
            var Q4;
            {var subQ0=sQuery(id+"F0.wireOp",EDGE,"E25.7");var subQ1=sQuery(id+"F0.wireOp",EDGE,"E25.1");var subQ2=sQuery(id+"F0.wireOp",EDGE,"E25.6");var subQ3=sQuery(id+"F0.wireOp",EDGE,"E25.5");var subQ4=sQuery(id+"F0.wireOp",EDGE,"E25.4");var subQ5=sQuery(id+"F0.wireOp",EDGE,"E25.0");var subQ6=sQuery(id+"F0.wireOp",EDGE,"E25.2");var subQ7=sQuery(id+"F0.wireOp",EDGE,"E25.3");Q4=makeQuery(id+"F8.boolean.opBoolean","INTERSECT",EDGE,{"derivedFrom":[makeQuery(id+"F5.boolean.opBoolean","SPLIT",FACE,{"disambiguationData":[TD([makeQuery(id+"F2.opExtrude","SWEPT_FACE",FACE,{"disambiguationData":[OSD([subQ5])]})])],"derivedFrom":makeQuery(id+"F3.boolean.opBoolean","COPY",FACE,{"derivedFrom":makeQuery(id+"F3.opExtrude","CAP_FACE",FACE,{"disambiguationData":[OSD([subQ5,subQ1,subQ6,subQ7,subQ4,subQ3,subQ2,subQ0])],"isStart":false})})}),makeQuery(id+"F8.opExtrude","SWEPT_FACE",FACE,{"disambiguationData":[OSD([sQuery(id+"F7.wireOp",EDGE,"E67")])]})]});}
            var Q5;
            Q5=makeQuery(id+"F8.boolean.opBoolean","INTERSECT",EDGE,{"disambiguationData":[OD(0.0)],"derivedFrom":[makeQuery(id+"F5.opExtrude","SWEPT_FACE",FACE,{"disambiguationData":[OSD([sQuery(id+"F4.wireOp",EDGE,"E30")])]}),makeQuery(id+"F8.opExtrude","SWEPT_FACE",FACE,{"disambiguationData":[OSD([sQuery(id+"F7.wireOp",EDGE,"E67")])]})]});
            fillet(context, id + "F14", {"entities" : qUnion([Q0, Q1, Q2, Q3, Q4, Q5]), "radius" : 3 * mm, "tangentPropagation" : true, "allowEdgeOverflow" : false});
        }
        {
            var Q0;
            Q0=makeQuery(id+"F1.opExtrude","CAP_EDGE",EDGE,{"disambiguationData":[OSD([sQuery(id+"F0.wireOp",EDGE,"E1.bottom")])],"isStart":false});
            fillet(context, id + "F15", {"entities" : qUnion([Q0]), "radius" : 2 * mm, "tangentPropagation" : true, "allowEdgeOverflow" : false});
        }
        {
            var Q0;
            {var subQ0=sQuery(id+"F0.wireOp",EDGE,"E21.filletArc");var subQ1=sQuery(id+"F0.wireOp",EDGE,"E7");var subQ2=sQuery(id+"F0.wireOp",EDGE,"E6");var subQ3=sQuery(id+"F0.wireOp",EDGE,"E5");var subQ4=sQuery(id+"F0.wireOp",EDGE,"E4");var subQ5=sQuery(id+"F0.wireOp",EDGE,"E22.filletArc");var subQ6=sQuery(id+"F0.wireOp",EDGE,"E1.bottom");var subQ7=sQuery(id+"F0.wireOp",EDGE,"E1.right");var subQ8=sQuery(id+"F0.wireOp",EDGE,"E1.top");var subQ9=sQuery(id+"F0.wireOp",EDGE,"E1.left");var subQ10=sQuery(id+"F0.wireOp",EDGE,"E23.filletArc");var subQ11=sQuery(id+"F0.wireOp",EDGE,"E24.filletArc");Q0=makeQuery(id+"F2.boolean.opBoolean","SPLIT",FACE,{"disambiguationData":[TD([makeQuery(id+"F1.opExtrude","SWEPT_FACE",FACE,{"disambiguationData":[OSD([subQ6])]})])],"derivedFrom":makeQuery(id+"F1.opExtrude","CAP_FACE",FACE,{"disambiguationData":[OSD([subQ6,subQ8,subQ9,subQ7,subQ4,subQ3,subQ2,subQ1,subQ0,subQ5,subQ10,subQ11])],"isStart":true})});}
            var sketch = newSketch(context, id + "F16", { "sketchPlane" : qUnion([Q0])});
            skLineSegment(sketch, "E79", {"start": v(0, 74.25) * mm, "end": v(0, 104.25) * mm, "construction": true});
            skArc(sketch, "E80", {"start": v(15, 104.25) * mm, "mid": v(0, 119.25) * mm, "end": v(-15, 104.25) * mm});
            skLineSegment(sketch, "E81", {"start": v(15, 104.25) * mm, "end": v(15, 92.25) * mm});
            skLineSegment(sketch, "E82", {"start": v(-15, 104.25) * mm, "end": v(-15, 92.25) * mm});
            skLineSegment(sketch, "E83", {"start": v(15, 92.25) * mm, "end": v(33, 74.25) * mm});
            skLineSegment(sketch, "E84", {"start": v(-15, 92.25) * mm, "end": v(-33, 74.25) * mm});
            skCircle(sketch, "E85", {"center": v(0, 104.25) * mm, "radius": 6 * mm});
            skLineSegment(sketch, "E86", {"start": v(-74.25, 0) * mm, "end": v(74.25, 0) * mm});
            skArc(sketch, "E87.MirrorCS", {"start": v(-15, 104.25) * mm, "mid": v(0, 119.25) * mm, "end": v(15, 104.25) * mm});
            skLineSegment(sketch, "E88.MirrorCS", {"start": v(15, -92.25) * mm, "end": v(33, -74.25) * mm});
            skLineSegment(sketch, "E89.MirrorCS", {"start": v(-15, -92.25) * mm, "end": v(-33, -74.25) * mm});
            skLineSegment(sketch, "E90.MirrorCS", {"start": v(-15, -104.25) * mm, "end": v(-15, -92.25) * mm});
            skLineSegment(sketch, "E91.MirrorCS", {"start": v(15, -104.25) * mm, "end": v(15, -92.25) * mm});
            skArc(sketch, "E92.MirrorCS", {"start": v(15, -104.25) * mm, "mid": v(0, -119.25) * mm, "end": v(-15, -104.25) * mm});
            skCircle(sketch, "E93.MirrorC", {"center": v(0, -104.25) * mm, "radius": 6 * mm});
            skArc(sketch, "E94.MirrorCS", {"start": v(-15, -104.25) * mm, "mid": v(0, -119.25) * mm, "end": v(15, -104.25) * mm});
            skLineSegment(sketch, "E95.MirrorCS", {"start": v(0, -74.25) * mm, "end": v(0, -104.25) * mm, "construction": true});
            skSolve(sketch);
        }
        {
            var Q0;
            {var subQ1=sQuery(id+"F16.wireOp",EDGE,"E84");Q0=makeQuery(id+"F16.imprint","IMPRINT",FACE,{"disambiguationData":[TD([[makeQuery(id+"F16.imprint","IMPRINT",EDGE,{"derivedFrom":subQ1}),1.0]])]});}
            var Q1;
            Q1=makeQuery(id+"F16.imprint","IMPRINT",FACE,{"disambiguationData":[TD([[makeQuery(id+"F16.imprint","IMPRINT",EDGE,{"derivedFrom":makeQuery(id+"F1.opExtrude","CAP_EDGE",EDGE,{"disambiguationData":[OSD([sQuery(id+"F0.wireOp",EDGE,"E4")])],"isStart":true})}),-1.0]])]});
            var Q2;
            Q2=makeQuery(id+"F16.imprint","IMPRINT",FACE,{"disambiguationData":[TD([[makeQuery(id+"F16.imprint","IMPRINT",EDGE,{"derivedFrom":makeQuery(id+"F1.opExtrude","CAP_EDGE",EDGE,{"disambiguationData":[OSD([sQuery(id+"F0.wireOp",EDGE,"E6")])],"isStart":true})}),-1.0]])]});
            var Q3;
            Q3=makeQuery(id+"F16.imprint","IMPRINT",FACE,{"disambiguationData":[TD([[makeQuery(id+"F16.imprint","IMPRINT",EDGE,{"derivedFrom":sQuery(id+"F16.wireOp",EDGE,"E91.MirrorCS")}),1.0]])]});
            var Q4;
            Q4=makeQuery(id+"F2.opExtrude","CAP_FACE",FACE,{"disambiguationData":[OSD([sQuery(id+"F0.wireOp",EDGE,"E12"),sQuery(id+"F0.wireOp",EDGE,"E13"),sQuery(id+"F0.wireOp",EDGE,"E14"),sQuery(id+"F0.wireOp",EDGE,"E15"),sQuery(id+"F0.wireOp",EDGE,"E17.filletArc"),sQuery(id+"F0.wireOp",EDGE,"E18.filletArc"),sQuery(id+"F0.wireOp",EDGE,"E19.filletArc"),sQuery(id+"F0.wireOp",EDGE,"E20.filletArc"),sQuery(id+"F0.wireOp",EDGE,"E25.0"),sQuery(id+"F0.wireOp",EDGE,"E25.1"),sQuery(id+"F0.wireOp",EDGE,"E25.2"),sQuery(id+"F0.wireOp",EDGE,"E25.3"),sQuery(id+"F0.wireOp",EDGE,"E25.4"),sQuery(id+"F0.wireOp",EDGE,"E25.5"),sQuery(id+"F0.wireOp",EDGE,"E25.6"),sQuery(id+"F0.wireOp",EDGE,"E25.7")])],"isStart":false});
            extrude(context, id + "F17", {"entities" : qUnion([Q0, Q1, Q2, Q3]), "endBound" : BoundingType.UP_TO_SURFACE, "endBoundEntityFace" : qUnion([Q4]), "depth" : 25 * mm});
        }
    });
